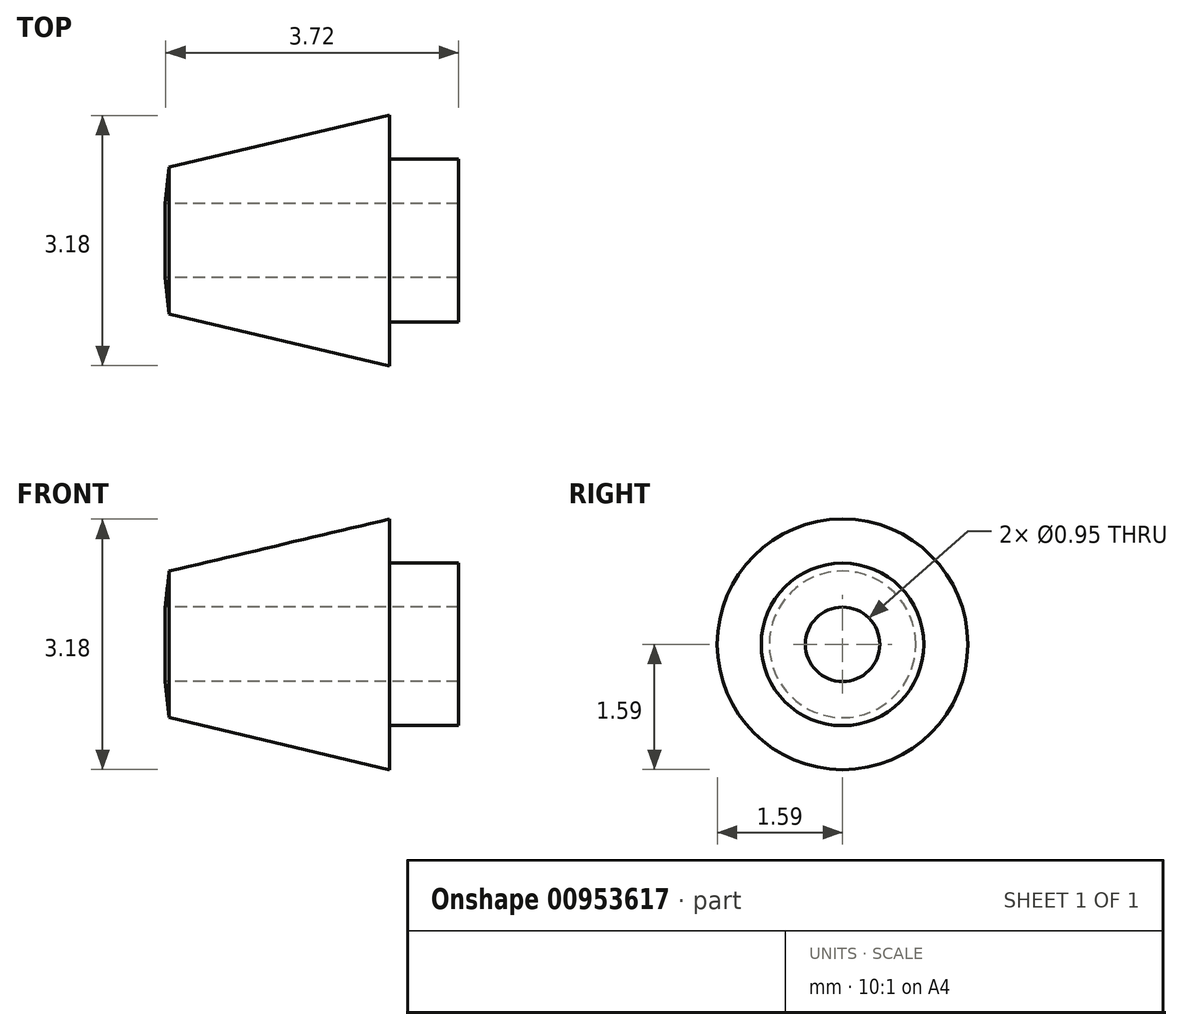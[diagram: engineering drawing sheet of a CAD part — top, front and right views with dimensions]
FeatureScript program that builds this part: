
annotation { "Feature Type Name" : "Feature", "Feature Type Description" : "" }
export const myFeature = defineFeature(function(context is Context, id is Id, definition is map)
    precondition{}
    {
        {
            var Q0;
            Q0=qCreatedBy(makeId("Front.planeOp"),FACE);
            var sketch = newSketch(context, id + "F0", { "sketchPlane" : qUnion([Q0])});
            skLineSegment(sketch, "E0", {"start": v(-1.53, 0.47) * mm, "end": v(1.31, 0.47) * mm});
            skLineSegment(sketch, "E1", {"start": v(1.31, 0.47) * mm, "end": v(1.31, 1.6) * mm});
            skLineSegment(sketch, "E2", {"start": v(-1.48, 0.93) * mm, "end": v(1.31, 1.6) * mm});
            skLineSegment(sketch, "E3", {"start": v(-1.48, 0.93) * mm, "end": v(-1.53, 0.47) * mm});
            skLineSegment(sketch, "E4", {"start": v(-2.67, 0) * mm, "end": v(2.66, 0) * mm});
            skLineSegment(sketch, "E5", {"start": v(1.31, 1.03) * mm, "end": v(2.2, 1.03) * mm});
            skLineSegment(sketch, "E6", {"start": v(2.2, 1.03) * mm, "end": v(2.2, 0.47) * mm});
            skLineSegment(sketch, "E7", {"start": v(2.2, 0.47) * mm, "end": v(1.31, 0.47) * mm});
            skSolve(sketch);
        }
        {
            var Q0;
            Q0 = qSketchRegion(id + "F0", true);
            var Q1;
            Q1=sQuery(id+"F0.wireOp",EDGE,"E4");
            revolve(context, id + "F1", {"surfaceOperationType" : NewSurfaceOperationType.NEW, "entities" : qUnion([Q0]), "axis" : qUnion([Q1]), "revolveType" : RevolveType.FULL});
        }
    });
